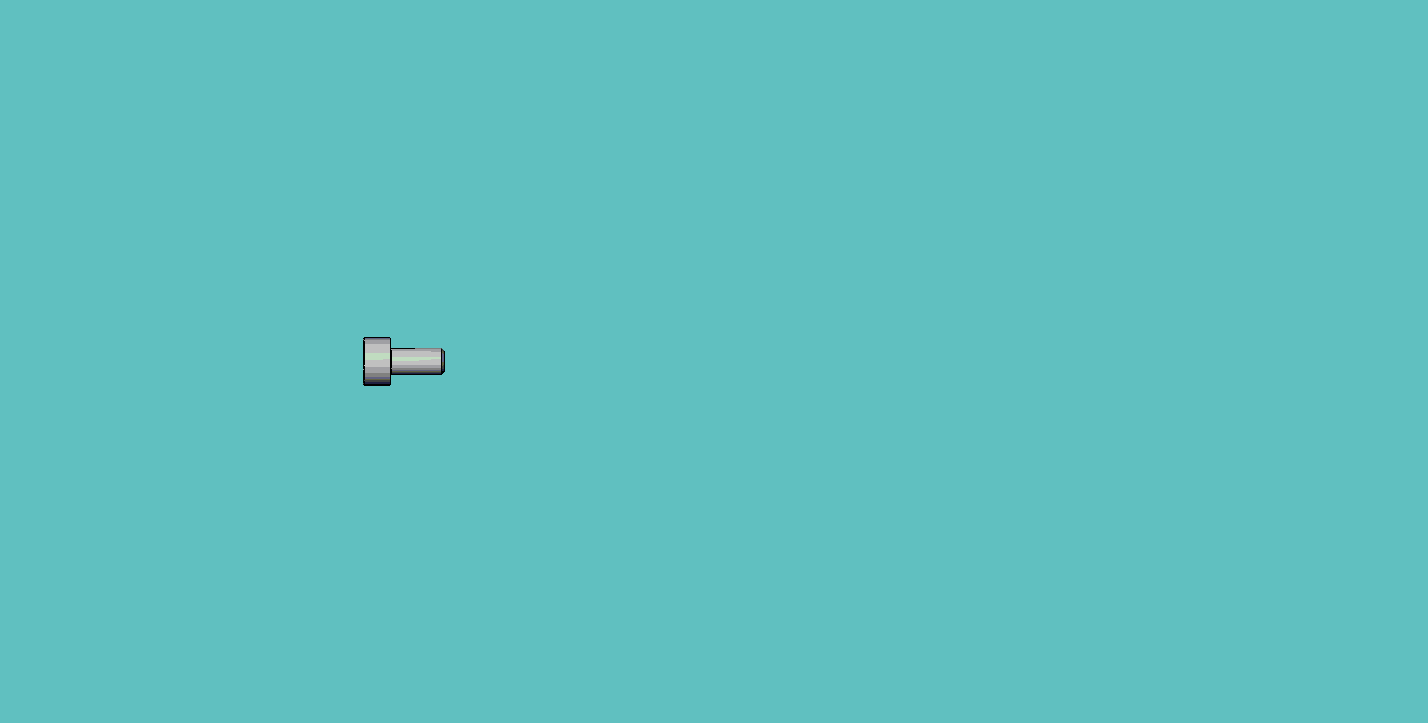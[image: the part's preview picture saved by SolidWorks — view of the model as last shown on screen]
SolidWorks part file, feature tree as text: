
SOLIDWORKS PART (.sldprt)
format: sldprt  version: not decoded by parser v0  size: 192,512 bytes
history: native  units: mm
features: sketch x4, plane x3, fillet x2, cut_revolve x2, material x1, revolve x1, thread x1, cut_extrude x1, pattern_linear x1 (+10 scaffold rows collapsed; 1 parser-record rows omitted)
feature tree (27):
  scaffold x10  (default folders/planes/origin — collapsed)
  material  "Material <not specified>"
  plane  "Plane1"
  plane  "Plane2"
  plane  "Plane3"
  parser-record x1  (decoder bookkeeping rows leaked as tree rows — omitted from the tree; the rows remain in map.json)
  revolve  "Base-Revolve"  [1 undecoded]
  sketch  "BodySke"  dims[c1.Head_fillet_rad=1.016mm c1.Head_top_radius=2.54mm c1.D1=19.05mm c1.Diameter=25.4mm c1.D3=50.8mm c1.D4=22.225mm c2.D4=45.0deg c2.D5=22.225mm c2.Head_ht=4.0mm c2.Length=8.0mm c2.D8=9.525mm c3.D8=45.0deg c3.D1=9.525mm c4.D8=9.525mm c5.D8=45.0deg c5.D1=73.025mm c6.D1=45.0deg c7.D1=9.525mm c8.D1=45.0deg c8.D4=22.225mm c9.D4=45.0deg c9.Thread_min=12.7mm c10.D4=9.525mm c10.Body_ch_ang=45.0deg c10.D8=22.225mm c11.D8=45.0deg c11.D5=22.225mm c12.D5=45.0deg c13.D5=~4.490128mm c14.D5=45.0deg c14.Head_dia=50.8mm c15.D5=~8.980256mm c15.Head_ch_ang=45.0deg c15.Head_side_ht=22.86mm c15.D9=19.05mm c15.Diameter=4.0mm c15.Head_dia=38.1mm c15.Minor_dia=3.22mm c15.Advance=0.7mm c15.Thread_nom=8.0mm c15.Thread_lim=~74.083342mm c15.Thread_length=60.0mm c16.Head_dia=7.0mm]
  thread  "ThreadCosmetic"  Diameter=5.9mm Thread_length=5.9mm Thread_minor=3.22mm  [1 undecoded]
  fillet  "Fillet1"  Radius=0.2mm Head_dia=7mm
  fillet  "Fillet2"  Radius=0.2mm
  sketch  "Sketch2"  dims[c1.D1=1.5355mm c1.D2=25.4mm c2.D2=60.0deg c2.Wall_thickness=11.427mm c2.Depth=2.0mm]
  cut_revolve  "Hex-PreBroach"  Angle=360deg
  sketch  "Sketch3"  dims[c1.D1=1.5355mm c1.D2=1.5355mm c1.Hex_size=3.071mm c1.D4=~14.664697mm c2.D4=120.0deg]
  cut_extrude  "Hex"  Depth=2mm Key_eng=2mm
  sketch  "ThdSchSke"  dims[c1.Thread_minor=~1.03886mm c1.Diameter=~1.413535mm c1.Start=~0.988134mm c1.D4=~4.446753mm c1.Vee=60.0deg c2.Thread_minor=~1.03886mm c2.Start=~2.540025mm c2.D1=~0.108159mm c2.D2=~0.108159mm c3.D1=~0.216319mm c3.SideAngle=55.0deg c3.D2=~0.216319mm c3.VeeAngle=70.0deg c3.Thread_minor=3.22mm c3.Overcut=5.0mm c3.Diameter=4.0mm c3.D6=~8.326268mm c4.D1=~8.326268mm c5.D1=90.0deg c5.Start=54.0mm c6.Start=6.1mm]
  cut_revolve  "ThreadSchematic"  Angle=360deg
  pattern_linear  "ThdSchPat"  Count1=9 Count2=1 Spacing1=0.655556mm Spacing2=50mm Num_threads=9 Advance=0.655556mm CopiedFlag=1
decode coverage: 11 of 12 modeling features carry decoded parameters
note: ~ marks probable driven/reference dimensions
note: 2 parameter values undecoded
note: suppression state not decoded; provenance and decode notes live in map.json
